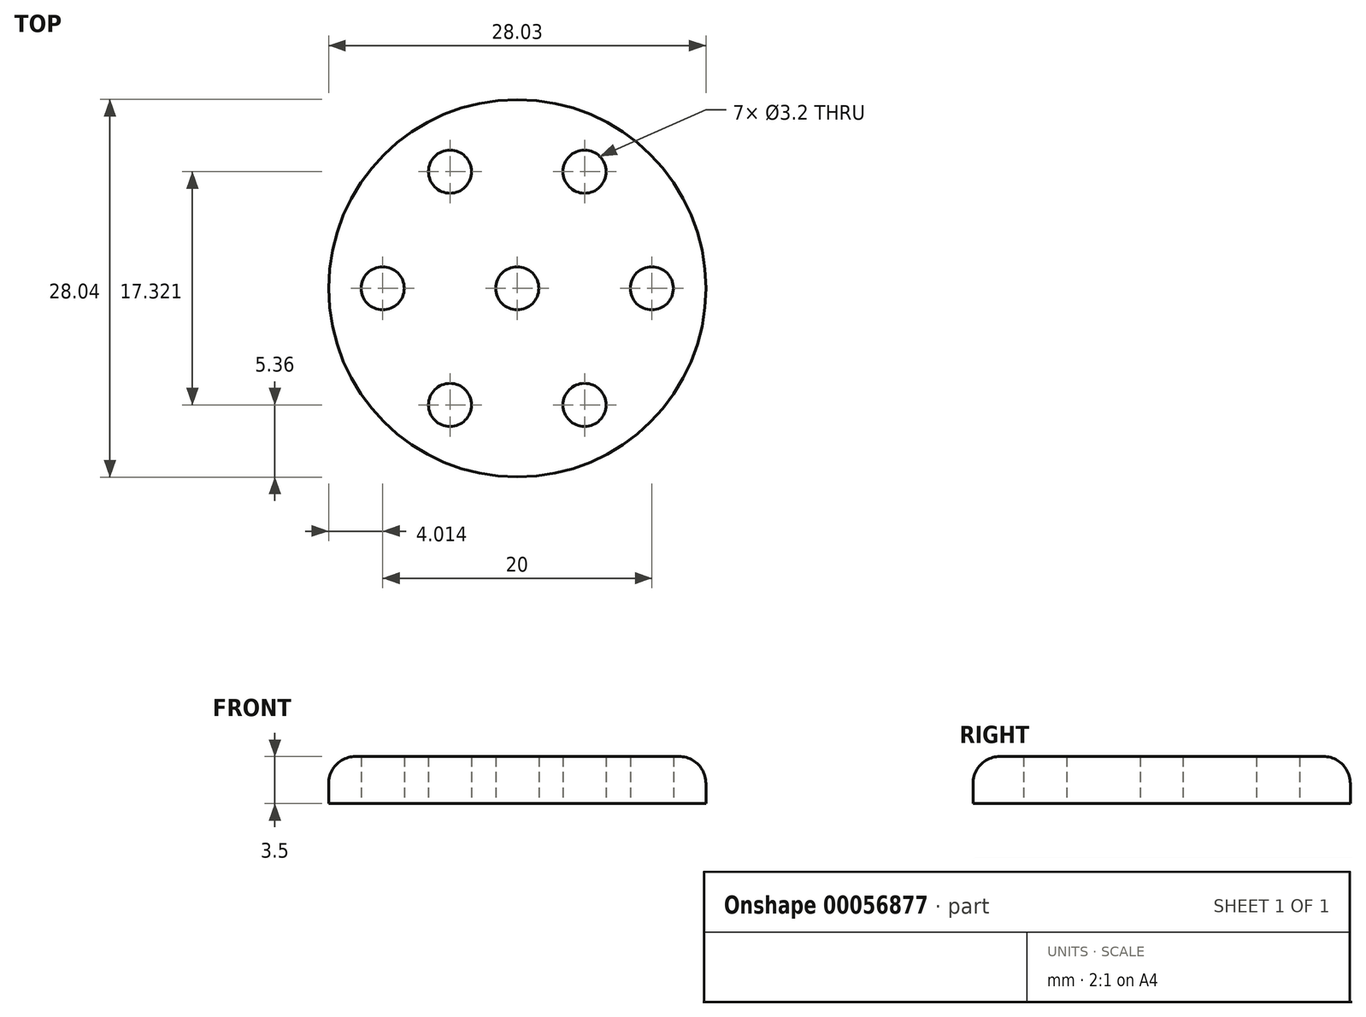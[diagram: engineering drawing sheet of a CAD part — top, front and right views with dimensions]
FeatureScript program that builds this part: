
annotation { "Feature Type Name" : "Feature", "Feature Type Description" : "" }
export const myFeature = defineFeature(function(context is Context, id is Id, definition is map)
    precondition{}
    {
        {
            var Q0;
            Q0=qCreatedBy(makeId("Top.planeOp"),FACE);
            var sketch = newSketch(context, id + "F0", { "sketchPlane" : qUnion([Q0])});
            skLineSegment(sketch, "E0.0", {"start": v(-12.83, 0) * mm, "end": v(21.17, 0) * mm, "construction": true});
            skLineSegment(sketch, "E1.0", {"start": v(3.17, 5) * mm, "end": v(3.17, -5) * mm, "construction": true});
            skLineSegment(sketch, "E2.0", {"start": v(14.17, 5) * mm, "end": v(14.17, -5) * mm, "construction": true});
            skCircle(sketch, "E3", {"center": v(4.17, 0) * mm, "radius": 1.6 * mm});
            skCircle(sketch, "E4", {"center": v(14.17, 0) * mm, "radius": 1.6 * mm});
            skPoint(sketch, "E5.center", {"position": v(-7.83, 0) * mm});
            skCircle(sketch, "E6.1.0", {"center": v(9.17, 8.66) * mm, "radius": 1.6 * mm});
            skCircle(sketch, "E6.2.0", {"center": v(-0.83, 8.66) * mm, "radius": 1.6 * mm});
            skCircle(sketch, "E6.3.0", {"center": v(-5.83, 0) * mm, "radius": 1.6 * mm});
            skCircle(sketch, "E6.4.0", {"center": v(-0.83, -8.66) * mm, "radius": 1.6 * mm});
            skCircle(sketch, "E6.5.0", {"center": v(9.17, -8.66) * mm, "radius": 1.6 * mm});
            skCircle(sketch, "E7", {"center": v(4.17, 0) * mm, "radius": 14.02 * mm});
            skSolve(sketch);
        }
        {
            var Q0;
            Q0=makeQuery(id+"F0.imprint","IMPRINT",FACE,{"disambiguationData":[TD([[makeQuery(id+"F0.imprint","IMPRINT",EDGE,{"derivedFrom":sQuery(id+"F0.wireOp",EDGE,"E5.2.0")}),-1.0]])]});
            var Q1;
            Q1=makeQuery(id+"F0.imprint","IMPRINT",FACE,{"disambiguationData":[TD([[makeQuery(id+"F0.imprint","IMPRINT",EDGE,{"derivedFrom":sQuery(id+"F0.wireOp",EDGE,"E3")}),-1.0]])]});
            extrude(context, id + "F1", {"entities" : qUnion([Q0, Q1]), "depth" : 3.5 * mm});
        }
        {
            var Q0;
            Q0=makeQuery(id+"F1.opExtrude","CAP_EDGE",EDGE,{"disambiguationData":[OSD([sQuery(id+"F0.wireOp",EDGE,"189e5b0c-76ec-412d-b71e-744613105145")])],"isStart":false});
            var Q1;
            Q1=makeQuery(id+"F1.opExtrude","CAP_EDGE",EDGE,{"disambiguationData":[OSD([sQuery(id+"F0.wireOp",EDGE,"ac196589-d03b-4877-baa9-04178efe06b0")])],"isStart":false});
            var Q2;
            Q2=makeQuery(id+"F1.opExtrude","CAP_EDGE",EDGE,{"disambiguationData":[OSD([sQuery(id+"F0.wireOp",EDGE,"E7")])],"isStart":false});
            fillet(context, id + "F2", {"entities" : qUnion([Q0, Q1, Q2]), "radius" : 2 * mm, "tangentPropagation" : true, "allowEdgeOverflow" : false});
        }
    });
